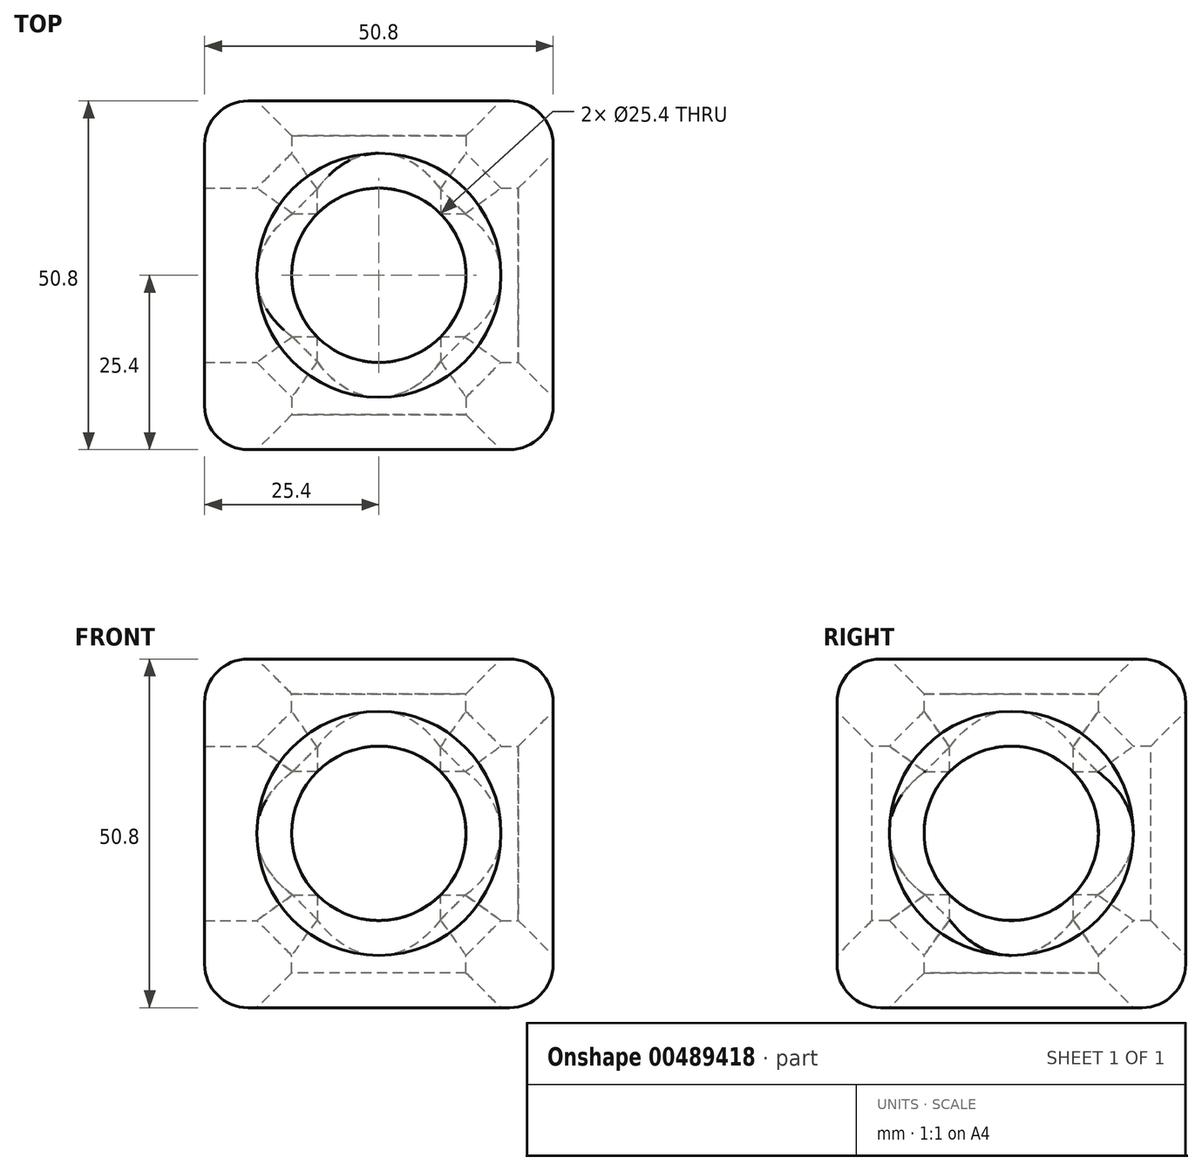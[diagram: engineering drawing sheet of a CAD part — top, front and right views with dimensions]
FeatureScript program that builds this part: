
annotation { "Feature Type Name" : "Feature", "Feature Type Description" : "" }
export const myFeature = defineFeature(function(context is Context, id is Id, definition is map)
    precondition{}
    {
        {
            var Q0;
            Q0=qCreatedBy(makeId("Front.planeOp"),FACE);
            var sketch = newSketch(context, id + "F0", { "sketchPlane" : qUnion([Q0])});
            skLineSegment(sketch, "E0", {"start": v(0, 0) * mm, "end": v(50.8, 0) * mm});
            skLineSegment(sketch, "E1", {"start": v(50.8, 0) * mm, "end": v(50.8, 50.8) * mm});
            skLineSegment(sketch, "E2", {"start": v(50.8, 50.8) * mm, "end": v(0, 50.8) * mm});
            skLineSegment(sketch, "E3", {"start": v(0, 50.8) * mm, "end": v(0, 0) * mm});
            skSolve(sketch);
        }
        {
            var Q0;
            Q0=makeQuery(id+"F0.imprint","IMPRINT",FACE,{"disambiguationData":[TD([[makeQuery(id+"F0.imprint","IMPRINT",EDGE,{"derivedFrom":sQuery(id+"F0.wireOp",EDGE,"E0")}),1.0]])]});
            extrude(context, id + "F1", {"entities" : qUnion([Q0]), "depth" : 50.8 * mm});
        }
        {
            var Q0;
            Q0=makeQuery(id+"F1.opExtrude","CAP_FACE",FACE,{"disambiguationData":[OSD([sQuery(id+"F0.wireOp",EDGE,"E0"),sQuery(id+"F0.wireOp",EDGE,"E1"),sQuery(id+"F0.wireOp",EDGE,"E2"),sQuery(id+"F0.wireOp",EDGE,"E3")])],"isStart":false});
            var sketch = newSketch(context, id + "F2", { "sketchPlane" : qUnion([Q0])});
            skCircle(sketch, "E4", {"center": v(25.4, 25.4) * mm, "radius": 12.7 * mm});
            skSolve(sketch);
        }
        {
            var Q0;
            Q0=makeQuery(id+"F2.imprint","IMPRINT",FACE,{"disambiguationData":[TD([[makeQuery(id+"F2.imprint","IMPRINT",EDGE,{"derivedFrom":sQuery(id+"F2.wireOp",EDGE,"E4")}),1.0]])]});
            extrude(context, id + "F3", {"entities" : qUnion([Q0]), "operationType" : NewBodyOperationType.REMOVE, "oppositeDirection" : true, "depth" : 50.8 * mm});
        }
        {
            var Q0;
            Q0=makeQuery(id+"F1.opExtrude","SWEPT_FACE",FACE,{"disambiguationData":[OSD([sQuery(id+"F0.wireOp",EDGE,"E1")])]});
            var sketch = newSketch(context, id + "F4", { "sketchPlane" : qUnion([Q0])});
            skCircle(sketch, "E5", {"center": v(-25.4, 25.4) * mm, "radius": 12.7 * mm});
            skSolve(sketch);
        }
        {
            var Q0;
            Q0=makeQuery(id+"F4.imprint","IMPRINT",FACE,{"disambiguationData":[TD([[makeQuery(id+"F4.imprint","IMPRINT",EDGE,{"derivedFrom":sQuery(id+"F4.wireOp",EDGE,"E5")}),1.0]])]});
            extrude(context, id + "F5", {"entities" : qUnion([Q0]), "operationType" : NewBodyOperationType.REMOVE, "oppositeDirection" : true, "depth" : 50.8 * mm});
        }
        {
            var Q0;
            Q0=makeQuery(id+"F1.opExtrude","SWEPT_FACE",FACE,{"disambiguationData":[OSD([sQuery(id+"F0.wireOp",EDGE,"E2")])]});
            var sketch = newSketch(context, id + "F6", { "sketchPlane" : qUnion([Q0])});
            skCircle(sketch, "E6", {"center": v(25.4, -25.4) * mm, "radius": 12.7 * mm});
            skSolve(sketch);
        }
        {
            var Q0;
            Q0=makeQuery(id+"F6.imprint","IMPRINT",FACE,{"disambiguationData":[TD([[makeQuery(id+"F6.imprint","IMPRINT",EDGE,{"derivedFrom":sQuery(id+"F6.wireOp",EDGE,"E6")}),1.0]])]});
            extrude(context, id + "F7", {"entities" : qUnion([Q0]), "operationType" : NewBodyOperationType.REMOVE, "oppositeDirection" : true, "depth" : 50.8 * mm});
        }
        {
            var Q0;
            Q0=makeQuery(id+"F7.boolean.opBoolean","COPY",FACE,{"disambiguationData":[TD([makeQuery(id+"F1.opExtrude","SWEPT_FACE",FACE,{"disambiguationData":[OSD([sQuery(id+"F0.wireOp",EDGE,"E2")])]})])],"derivedFrom":makeQuery(id+"F7.opExtrude","SWEPT_FACE",FACE,{"disambiguationData":[OSD([sQuery(id+"F6.wireOp",EDGE,"E6")])]})});
            var Q1;
            {var subQ0=makeQuery(id+"F3.boolean.opBoolean","COPY",FACE,{"derivedFrom":makeQuery(id+"F3.opExtrude","SWEPT_FACE",FACE,{"disambiguationData":[OSD([sQuery(id+"F2.wireOp",EDGE,"E4")])]})});Q1=makeQuery(id+"F5.boolean.opBoolean","SPLIT",FACE,{"disambiguationData":[TD([makeQuery(id+"F1.opExtrude","CAP_FACE",FACE,{"disambiguationData":[OSD([sQuery(id+"F0.wireOp",EDGE,"E0"),sQuery(id+"F0.wireOp",EDGE,"E1"),sQuery(id+"F0.wireOp",EDGE,"E2"),sQuery(id+"F0.wireOp",EDGE,"E3")])],"isStart":false})])],"derivedFrom":subQ0});}
            var Q2;
            Q2=makeQuery(id+"F7.boolean.opBoolean","COPY",FACE,{"disambiguationData":[TD([makeQuery(id+"F1.opExtrude","SWEPT_FACE",FACE,{"disambiguationData":[OSD([sQuery(id+"F0.wireOp",EDGE,"E0")])]})])],"derivedFrom":makeQuery(id+"F7.opExtrude","SWEPT_FACE",FACE,{"disambiguationData":[OSD([sQuery(id+"F6.wireOp",EDGE,"E6")])]})});
            var Q3;
            {var subQ0=makeQuery(id+"F3.boolean.opBoolean","COPY",FACE,{"derivedFrom":makeQuery(id+"F3.opExtrude","SWEPT_FACE",FACE,{"disambiguationData":[OSD([sQuery(id+"F2.wireOp",EDGE,"E4")])]})});Q3=makeQuery(id+"F5.boolean.opBoolean","SPLIT",FACE,{"disambiguationData":[TD([makeQuery(id+"F1.opExtrude","CAP_FACE",FACE,{"disambiguationData":[OSD([sQuery(id+"F0.wireOp",EDGE,"E0"),sQuery(id+"F0.wireOp",EDGE,"E1"),sQuery(id+"F0.wireOp",EDGE,"E2"),sQuery(id+"F0.wireOp",EDGE,"E3")])],"isStart":true})])],"derivedFrom":subQ0});}
            var Q4;
            {var subQ0=makeQuery(id+"F5.opExtrude","SWEPT_FACE",FACE,{"disambiguationData":[OSD([sQuery(id+"F4.wireOp",EDGE,"E5")])]});Q4=makeQuery(id+"F5.boolean.opBoolean","COPY",FACE,{"disambiguationData":[TD([makeQuery(id+"F1.opExtrude","SWEPT_FACE",FACE,{"disambiguationData":[OSD([sQuery(id+"F0.wireOp",EDGE,"E1")])]})])],"derivedFrom":subQ0});}
            chamfer(context, id + "F8", {"entities" : qUnion([Q0, Q1, Q2, Q3, Q4]), "width" : 5.08 * mm, "tangentPropagation" : true});
        }
        {
            var Q0;
            Q0=makeQuery(id+"F1.opExtrude","CAP_EDGE",EDGE,{"disambiguationData":[OSD([sQuery(id+"F0.wireOp",EDGE,"E2")])],"isStart":false});
            var Q1;
            Q1=makeQuery(id+"F1.opExtrude","SWEPT_EDGE",EDGE,{"disambiguationData":[OSD([sQuery(id+"F0.wireOp",EDGE,"E1"),sQuery(id+"F0.wireOp",EDGE,"E2")])]});
            var Q2;
            Q2=makeQuery(id+"F1.opExtrude","CAP_EDGE",EDGE,{"disambiguationData":[OSD([sQuery(id+"F0.wireOp",EDGE,"E1")])],"isStart":false});
            var Q3;
            Q3=makeQuery(id+"F1.opExtrude","CAP_EDGE",EDGE,{"disambiguationData":[OSD([sQuery(id+"F0.wireOp",EDGE,"E0")])],"isStart":false});
            var Q4;
            Q4=makeQuery(id+"F1.opExtrude","SWEPT_EDGE",EDGE,{"disambiguationData":[OSD([sQuery(id+"F0.wireOp",EDGE,"E0"),sQuery(id+"F0.wireOp",EDGE,"E1")])]});
            var Q5;
            Q5=makeQuery(id+"F1.opExtrude","CAP_EDGE",EDGE,{"disambiguationData":[OSD([sQuery(id+"F0.wireOp",EDGE,"E1")])],"isStart":true});
            var Q6;
            Q6=makeQuery(id+"F1.opExtrude","SWEPT_EDGE",EDGE,{"disambiguationData":[OSD([sQuery(id+"F0.wireOp",EDGE,"E2"),sQuery(id+"F0.wireOp",EDGE,"E3")])]});
            var Q7;
            Q7=makeQuery(id+"F1.opExtrude","CAP_EDGE",EDGE,{"disambiguationData":[OSD([sQuery(id+"F0.wireOp",EDGE,"E3")])],"isStart":false});
            var Q8;
            Q8=makeQuery(id+"F1.opExtrude","CAP_EDGE",EDGE,{"disambiguationData":[OSD([sQuery(id+"F0.wireOp",EDGE,"E2")])],"isStart":true});
            var Q9;
            Q9=makeQuery(id+"F1.opExtrude","CAP_EDGE",EDGE,{"disambiguationData":[OSD([sQuery(id+"F0.wireOp",EDGE,"E3")])],"isStart":true});
            var Q10;
            Q10=makeQuery(id+"F1.opExtrude","SWEPT_EDGE",EDGE,{"disambiguationData":[OSD([sQuery(id+"F0.wireOp",EDGE,"E0"),sQuery(id+"F0.wireOp",EDGE,"E3")])]});
            var Q11;
            Q11=makeQuery(id+"F1.opExtrude","CAP_EDGE",EDGE,{"disambiguationData":[OSD([sQuery(id+"F0.wireOp",EDGE,"E0")])],"isStart":true});
            fillet(context, id + "F9", {"entities" : qUnion([Q0, Q1, Q2, Q3, Q4, Q5, Q6, Q7, Q8, Q9, Q10, Q11]), "radius" : 6.35 * mm, "tangentPropagation" : true, "allowEdgeOverflow" : false});
        }
    });
